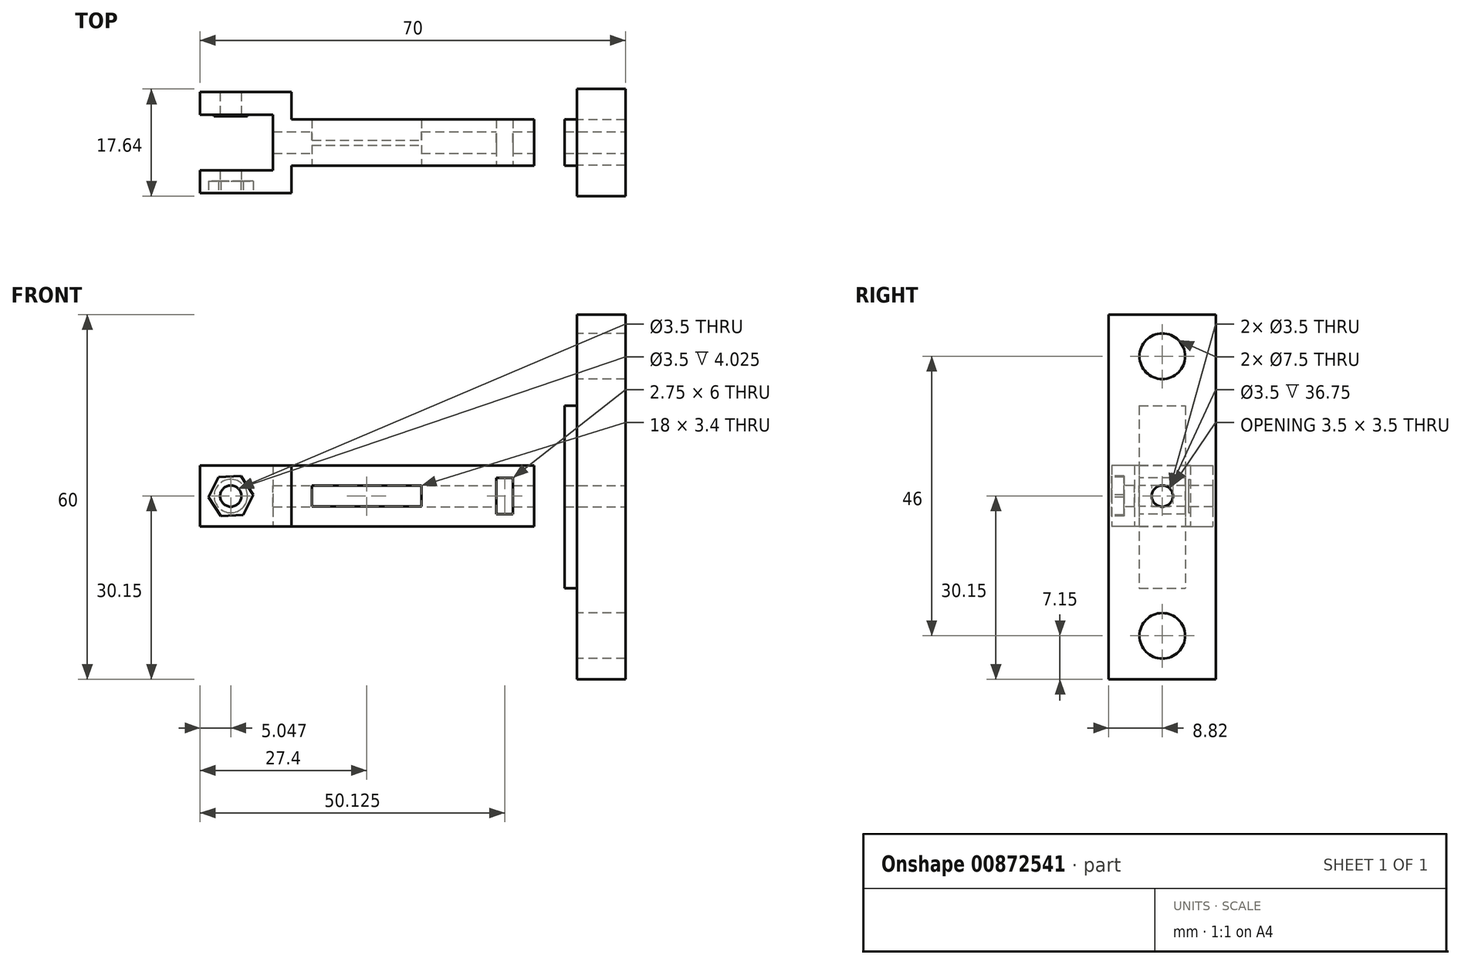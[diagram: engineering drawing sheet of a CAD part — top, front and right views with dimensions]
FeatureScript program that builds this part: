
annotation { "Feature Type Name" : "Feature", "Feature Type Description" : "" }
export const myFeature = defineFeature(function(context is Context, id is Id, definition is map)
    precondition{}
    {
        {
            var Q0;
            Q0=qCreatedBy(makeId("Top.planeOp"),FACE);
            var sketch = newSketch(context, id + "F0", { "sketchPlane" : qUnion([Q0])});
            skLineSegment(sketch, "E0.bottom", {"start": v(0, 0) * mm, "end": v(40, 0) * mm});
            skLineSegment(sketch, "E0.top", {"start": v(0, -3.83) * mm, "end": v(40, -3.83) * mm});
            skLineSegment(sketch, "E0.left", {"start": v(0, 0) * mm, "end": v(0, -3.83) * mm});
            skLineSegment(sketch, "E0.right", {"start": v(40, 0) * mm, "end": v(40, -3.83) * mm});
            skLineSegment(sketch, "E1.bottom", {"start": v(-3, 0) * mm, "end": v(0, 0) * mm});
            skLineSegment(sketch, "E1.top", {"start": v(-15, -8.32) * mm, "end": v(0, -8.32) * mm});
            skLineSegment(sketch, "E1.left", {"start": v(-15, -4.6) * mm, "end": v(-15, -8.32) * mm});
            skLineSegment(sketch, "E1.right", {"start": v(0, 0) * mm, "end": v(0, -8.32) * mm});
            skLineSegment(sketch, "E2.top", {"start": v(-15, -4.6) * mm, "end": v(-3, -4.6) * mm});
            skLineSegment(sketch, "E2.right", {"start": v(-3, 0) * mm, "end": v(-3, -4.6) * mm});
            skLineSegment(sketch, "E3.MirrorCS", {"start": v(0, 0) * mm, "end": v(0, 3.83) * mm});
            skLineSegment(sketch, "E4.MirrorCS", {"start": v(0, 0) * mm, "end": v(0, 8.32) * mm});
            skLineSegment(sketch, "E5.MirrorCS", {"start": v(-15, 4.6) * mm, "end": v(-15, 8.32) * mm});
            skLineSegment(sketch, "E6.MirrorCS", {"start": v(-3, 0) * mm, "end": v(-3, 4.6) * mm});
            skLineSegment(sketch, "E7.MirrorCS", {"start": v(-15, 8.32) * mm, "end": v(0, 8.32) * mm});
            skLineSegment(sketch, "E8.MirrorCS", {"start": v(-15, 4.6) * mm, "end": v(-3, 4.6) * mm});
            skLineSegment(sketch, "E9.MirrorCS", {"start": v(40, 0) * mm, "end": v(40, 3.83) * mm});
            skLineSegment(sketch, "E10.MirrorCS", {"start": v(0, 3.83) * mm, "end": v(40, 3.83) * mm});
            skSolve(sketch);
        }
        {
            var Q0;
            Q0=makeQuery(id+"F0.imprint","IMPRINT",FACE,{"disambiguationData":[TD([[makeQuery(id+"F0.imprint","IMPRINT",EDGE,{"derivedFrom":sQuery(id+"F0.wireOp",EDGE,"E0.left")}),-1.0]])]});
            var Q1;
            Q1=makeQuery(id+"F0.imprint","IMPRINT",FACE,{"disambiguationData":[TD([[makeQuery(id+"F0.imprint","IMPRINT",EDGE,{"derivedFrom":sQuery(id+"F0.wireOp",EDGE,"E1.bottom")}),1.0]])]});
            var Q2;
            Q2=makeQuery(id+"F0.imprint","IMPRINT",FACE,{"disambiguationData":[TD([[makeQuery(id+"F0.imprint","IMPRINT",EDGE,{"derivedFrom":sQuery(id+"F0.wireOp",EDGE,"E0.bottom")}),1.0]])]});
            var Q3;
            Q3=makeQuery(id+"F0.imprint","IMPRINT",FACE,{"disambiguationData":[TD([[makeQuery(id+"F0.imprint","IMPRINT",EDGE,{"derivedFrom":sQuery(id+"F0.wireOp",EDGE,"E0.bottom")}),-1.0]])]});
            extrude(context, id + "F1", {"entities" : qUnion([Q0, Q1, Q2, Q3]), "depth" : 10 * mm});
        }
        {
            var Q0;
            Q0=makeQuery(id+"F1.opExtrude","SWEPT_FACE",FACE,{"disambiguationData":[OSD([sQuery(id+"F0.wireOp",EDGE,"E1.top")])]});
            var sketch = newSketch(context, id + "F2", { "sketchPlane" : qUnion([Q0])});
            skCircle(sketch, "E11", {"center": v(-9.95, 5) * mm, "radius": 1.75 * mm});
            skSolve(sketch);
        }
        {
            var Q0;
            Q0=makeQuery(id+"F2.imprint","IMPRINT",FACE,{"disambiguationData":[TD([[makeQuery(id+"F2.imprint","IMPRINT",EDGE,{"derivedFrom":sQuery(id+"F2.wireOp",EDGE,"E11")}),1.0]])]});
            extrude(context, id + "F3", {"entities" : qUnion([Q0]), "operationType" : NewBodyOperationType.REMOVE, "endBound" : BoundingType.THROUGH_ALL, "oppositeDirection" : true, "depth" : 25 * mm});
        }
        {
            var Q0;
            Q0=makeQuery(id+"F1.opExtrude","SWEPT_FACE",FACE,{"disambiguationData":[OSD([sQuery(id+"F0.wireOp",EDGE,"E0.top")])]});
            var sketch = newSketch(context, id + "F4", { "sketchPlane" : qUnion([Q0])});
            skLineSegment(sketch, "E12.bottom", {"start": v(3.4, 3.3) * mm, "end": v(21.4, 3.3) * mm});
            skLineSegment(sketch, "E12.top", {"start": v(3.4, 6.7) * mm, "end": v(21.4, 6.7) * mm});
            skLineSegment(sketch, "E12.left", {"start": v(3.4, 3.3) * mm, "end": v(3.4, 6.7) * mm});
            skLineSegment(sketch, "E12.right", {"start": v(21.4, 3.3) * mm, "end": v(21.4, 6.7) * mm});
            skLineSegment(sketch, "E13.bottom", {"start": v(33.75, 8) * mm, "end": v(36.5, 8) * mm});
            skLineSegment(sketch, "E13.top", {"start": v(33.75, 2) * mm, "end": v(36.5, 2) * mm});
            skLineSegment(sketch, "E13.left", {"start": v(33.75, 8) * mm, "end": v(33.75, 2) * mm});
            skLineSegment(sketch, "E13.right", {"start": v(36.5, 8) * mm, "end": v(36.5, 2) * mm});
            skSolve(sketch);
        }
        {
            var Q0;
            Q0=makeQuery(id+"F4.imprint","IMPRINT",FACE,{"disambiguationData":[TD([[makeQuery(id+"F4.imprint","IMPRINT",EDGE,{"derivedFrom":sQuery(id+"F4.wireOp",EDGE,"E12.bottom")}),1.0]])]});
            var Q1;
            Q1=makeQuery(id+"F4.imprint","IMPRINT",FACE,{"disambiguationData":[TD([[makeQuery(id+"F4.imprint","IMPRINT",EDGE,{"derivedFrom":sQuery(id+"F4.wireOp",EDGE,"E13.bottom")}),-1.0]])]});
            extrude(context, id + "F5", {"entities" : qUnion([Q0, Q1]), "operationType" : NewBodyOperationType.REMOVE, "endBound" : BoundingType.THROUGH_ALL, "oppositeDirection" : true, "depth" : 25 * mm});
        }
        {
            var Q0;
            Q0=makeQuery(id+"F1.opExtrude","SWEPT_FACE",FACE,{"disambiguationData":[OSD([sQuery(id+"F0.wireOp",EDGE,"E0.right"),sQuery(id+"F0.wireOp",EDGE,"E9.MirrorCS")])]});
            var sketch = newSketch(context, id + "F6", { "sketchPlane" : qUnion([Q0])});
            skCircle(sketch, "E14", {"center": v(0, 5) * mm, "radius": 1.75 * mm});
            skSolve(sketch);
        }
        {
            var Q0;
            Q0=makeQuery(id+"F6.imprint","IMPRINT",FACE,{"disambiguationData":[TD([[makeQuery(id+"F6.imprint","IMPRINT",EDGE,{"derivedFrom":sQuery(id+"F6.wireOp",EDGE,"E14")}),1.0]])]});
            extrude(context, id + "F7", {"entities" : qUnion([Q0]), "operationType" : NewBodyOperationType.REMOVE, "oppositeDirection" : true, "depth" : 15 * mm});
        }
        {
            var Q0;
            Q0=makeQuery(id+"F1.opExtrude","SWEPT_FACE",FACE,{"disambiguationData":[OSD([sQuery(id+"F0.wireOp",EDGE,"E0.right"),sQuery(id+"F0.wireOp",EDGE,"E9.MirrorCS")])]});
            cPlane(context, id + "F8", {"entities" : qUnion([Q0]), "cplaneType" : CPlaneType.OFFSET, "offset" : 5 * mm, "width" : 150 * mm, "height" : 150 * mm});
        }
        {
            var Q0;
            Q0=qCreatedBy(id+"F8.planeOp",FACE);
            var sketch = newSketch(context, id + "F9", { "sketchPlane" : qUnion([Q0])});
            skLineSegment(sketch, "E15.0", {"start": v(3.83, 10) * mm, "end": v(3.83, 0) * mm});
            skLineSegment(sketch, "E16.0", {"start": v(-3.83, 10) * mm, "end": v(-3.83, 0) * mm});
            skLineSegment(sketch, "E17.bottom", {"start": v(-3.82, 19.85) * mm, "end": v(3.82, 19.85) * mm});
            skLineSegment(sketch, "E17.top", {"start": v(-3.82, -10.15) * mm, "end": v(3.82, -10.15) * mm});
            skLineSegment(sketch, "E17.left", {"start": v(-3.83, 19.85) * mm, "end": v(-3.82, -10.15) * mm});
            skLineSegment(sketch, "E17.right", {"start": v(3.82, 19.85) * mm, "end": v(3.83, -10.15) * mm});
            skPoint(sketch, "E18.oppositeSnap0", {"position": v(3.83, 4.85) * mm});
            skLineSegment(sketch, "E18.bottom", {"start": v(3.83, 4.85) * mm, "end": v(3.83, 4.85) * mm});
            skLineSegment(sketch, "E18.top", {"start": v(3.83, 4.85) * mm, "end": v(3.83, 4.85) * mm});
            skLineSegment(sketch, "E18.left", {"start": v(3.83, 4.85) * mm, "end": v(3.83, 4.85) * mm});
            skLineSegment(sketch, "E18.right", {"start": v(3.83, 4.85) * mm, "end": v(3.83, 4.85) * mm});
            skSolve(sketch);
        }
        {
            var Q0;
            {var subQ0=sQuery(id+"F9.wireOp",EDGE,"E17.bottom");Q0=makeQuery(id+"F9.imprint","IMPRINT",FACE,{"disambiguationData":[TD([[makeQuery(id+"F9.imprint","IMPRINT",EDGE,{"derivedFrom":subQ0}),-1.0]])]});}
            extrude(context, id + "F10", {"entities" : qUnion([Q0]), "depth" : 2 * mm});
        }
        {
            var Q0;
            Q0=makeQuery(id+"F10.opExtrude","CAP_FACE",FACE,{"disambiguationData":[OSD([sQuery(id+"F9.wireOp",EDGE,"E17.bottom"),sQuery(id+"F9.wireOp",EDGE,"E17.top"),sQuery(id+"F9.wireOp",EDGE,"E17.left"),sQuery(id+"F9.wireOp",EDGE,"E17.right")])],"isStart":false});
            var sketch = newSketch(context, id + "F11", { "sketchPlane" : qUnion([Q0])});
            skLineSegment(sketch, "E19.bottom", {"start": v(8.82, 34.85) * mm, "end": v(-8.83, 34.85) * mm});
            skLineSegment(sketch, "E19.top", {"start": v(8.83, -25.15) * mm, "end": v(-8.82, -25.15) * mm});
            skLineSegment(sketch, "E19.left", {"start": v(8.82, 34.85) * mm, "end": v(8.83, -25.15) * mm});
            skLineSegment(sketch, "E19.right", {"start": v(-8.83, 34.85) * mm, "end": v(-8.82, -25.15) * mm});
            skSolve(sketch);
        }
        {
            var Q0;
            Q0=qSketchRegion(id+"F11",true);
            extrude(context, id + "F12", {"entities" : qUnion([Q0]), "operationType" : NewBodyOperationType.ADD, "depth" : 8 * mm});
        }
        {
            var Q0;
            Q0=makeQuery(id+"F12.opExtrude","CAP_FACE",FACE,{"disambiguationData":[OSD([sQuery(id+"F11.wireOp",EDGE,"E19.bottom"),sQuery(id+"F11.wireOp",EDGE,"E19.top"),sQuery(id+"F11.wireOp",EDGE,"E19.left"),sQuery(id+"F11.wireOp",EDGE,"E19.right")])],"isStart":false});
            var sketch = newSketch(context, id + "F13", { "sketchPlane" : qUnion([Q0])});
            skCircle(sketch, "E20.0", {"center": v(0, 5) * mm, "radius": 1.75 * mm});
            skSolve(sketch);
        }
        {
            var Q0;
            Q0=makeQuery(id+"F13.imprint","IMPRINT",FACE,{"disambiguationData":[TD([[makeQuery(id+"F13.imprint","IMPRINT",EDGE,{"derivedFrom":sQuery(id+"F13.wireOp",EDGE,"E20.0")}),1.0]])]});
            extrude(context, id + "F14", {"entities" : qUnion([Q0]), "operationType" : NewBodyOperationType.REMOVE, "endBound" : BoundingType.THROUGH_ALL, "oppositeDirection" : true, "depth" : 25 * mm});
        }
        {
            var Q0;
            Q0=makeQuery(id+"F1.opExtrude","SWEPT_FACE",FACE,{"disambiguationData":[OSD([sQuery(id+"F0.wireOp",EDGE,"E8.MirrorCS")])]});
            var sketch = newSketch(context, id + "F15", { "sketchPlane" : qUnion([Q0])});
            skCircle(sketch, "E21", {"center": v(-9.95, 5) * mm, "radius": 1.75 * mm});
            skCircle(sketch, "E22", {"center": v(-9.95, 5) * mm, "radius": 2.75 * mm});
            skSolve(sketch);
        }
        {
            var Q0;
            Q0=makeQuery(id+"F15.imprint","IMPRINT",FACE,{"disambiguationData":[TD([[makeQuery(id+"F15.imprint","IMPRINT",EDGE,{"derivedFrom":sQuery(id+"F15.wireOp",EDGE,"E21")}),1.0]])]});
            extrude(context, id + "F16", {"entities" : qUnion([Q0]), "operationType" : NewBodyOperationType.ADD, "depth" : 0.3 * mm});
        }
        {
            var Q0;
            Q0=makeQuery(id+"F1.opExtrude","SWEPT_FACE",FACE,{"disambiguationData":[OSD([sQuery(id+"F0.wireOp",EDGE,"E1.top")])]});
            var sketch = newSketch(context, id + "F17", { "sketchPlane" : qUnion([Q0])});
            skCircle(sketch, "E23.cCircle", {"center": v(-9.95, 5) * mm, "radius": 3.2 * mm, "construction": true});
            skLineSegment(sketch, "E23.0", {"start": v(-6.26, 5.2) * mm, "end": v(-7.93, 1.9) * mm});
            skLineSegment(sketch, "E23.1", {"start": v(-7.93, 1.9) * mm, "end": v(-11.62, 1.7) * mm});
            skLineSegment(sketch, "E23.2", {"start": v(-11.62, 1.7) * mm, "end": v(-13.64, 4.8) * mm});
            skLineSegment(sketch, "E23.3", {"start": v(-13.64, 4.8) * mm, "end": v(-11.98, 8.1) * mm});
            skLineSegment(sketch, "E23.4", {"start": v(-11.98, 8.1) * mm, "end": v(-8.29, 8.3) * mm});
            skLineSegment(sketch, "E23.5", {"start": v(-8.29, 8.3) * mm, "end": v(-6.26, 5.2) * mm});
            skPoint(sketch, "E23.0.midPoint", {"position": v(-7.1, 3.56) * mm});
            skSolve(sketch);
        }
        {
            var Q0;
            Q0=makeQuery(id+"F17.imprint","IMPRINT",FACE,{"disambiguationData":[TD([[makeQuery(id+"F17.imprint","IMPRINT",EDGE,{"derivedFrom":sQuery(id+"F17.wireOp",EDGE,"E23.0")}),-1.0]])]});
            extrude(context, id + "F18", {"entities" : qUnion([Q0]), "operationType" : NewBodyOperationType.REMOVE, "oppositeDirection" : true, "depth" : 2 * mm});
        }
        {
            var Q0;
            Q0=makeQuery(id+"F12.opExtrude","CAP_FACE",FACE,{"disambiguationData":[OSD([sQuery(id+"F11.wireOp",EDGE,"E19.bottom"),sQuery(id+"F11.wireOp",EDGE,"E19.top"),sQuery(id+"F11.wireOp",EDGE,"E19.left"),sQuery(id+"F11.wireOp",EDGE,"E19.right")])],"isStart":true});
            var sketch = newSketch(context, id + "F19", { "sketchPlane" : qUnion([Q0])});
            skCircle(sketch, "E24.0", {"center": v(0, 5) * mm, "radius": 1.75 * mm});
            skCircle(sketch, "E25", {"center": v(0, -18) * mm, "radius": 3.75 * mm});
            skCircle(sketch, "E26", {"center": v(0, 28) * mm, "radius": 3.75 * mm});
            skSolve(sketch);
        }
        {
            var Q0;
            Q0=sQuery(id+"F19.wireOp",VERTEX,"E25.center");
            var Q1;
            Q1=sQuery(id+"F19.wireOp",VERTEX,"E26.center");
            var Q2;
            Q2=makeQuery(id+"F10.opExtrude","SWEPT_BODY",BODY,{"disambiguationData":[OSD([sQuery(id+"F9.wireOp",EDGE,"E17.bottom"),sQuery(id+"F9.wireOp",EDGE,"E17.top"),sQuery(id+"F9.wireOp",EDGE,"E17.left"),sQuery(id+"F9.wireOp",EDGE,"E17.right")])]});
            hole(context, id + "F20", {"style" : HoleStyle.SIMPLE, "endStyle" : HoleEndStyle.THROUGH, "holeDiameter" : 7.5 * mm, "isTappedThrough" : true, "tappedDepth" : 12 * mm, "tapClearance" : 3, "locations" : qUnion([Q0, Q1]), "scope" : qUnion([Q2])});
        }
    });
